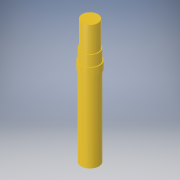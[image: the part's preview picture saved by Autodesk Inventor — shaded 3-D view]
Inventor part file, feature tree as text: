
AUTODESK INVENTOR PART (.ipt)
format: ipt  version: 2019 (Build 230136000, 136)  size: 129,024 bytes
history: native  units: in
note: dims shown in document units (in); Inventor stores cm internally (conversion verified against a paired STEP export)
features: extrude x5, sketch x5, projected_geometry x4
ambient origin geometry x8: Origin, YZ Plane, XZ Plane, XY Plane, X Axis, Y Axis, Z Axis, Center Point
bodies: Solid1 (feature_tree)
feature tree (14):
  extrude  "Extrusion1"  Depth=0.3435in TaperAngle=0.0deg
  extrude  "Extrusion2"  Depth=0.0315in TaperAngle=0.0deg
  extrude  "Extrusion3"  Depth=0.045in TaperAngle=0.0deg
  extrude  "Extrusion4"  Depth=0.1075in TaperAngle=0.0deg
  extrude  "Extrusion5"  Depth=0.3in TaperAngle=0.0deg
  sketch  "Sketch1"  dims[d0=0.075in d1=0.3435in d2=0.0in]
  sketch  "Sketch2"  dims[d3=0.0835in d4=0.0315in d5=0.0in]
  projected_geometry  "Projected Loop1"
  sketch  "Sketch3"  dims[d6=0.0695in d7=0.045in d8=0.0in]
  projected_geometry  "Projected Loop2"
  sketch  "Sketch4"  dims[d9=0.0675in d10=0.1075in d11=0.0in]
  projected_geometry  "Projected Loop3"
  sketch  "Sketch5"  dims[d12=0.045in d13=0.3in d14=0.0in]
  projected_geometry  "Projected Loop4"
